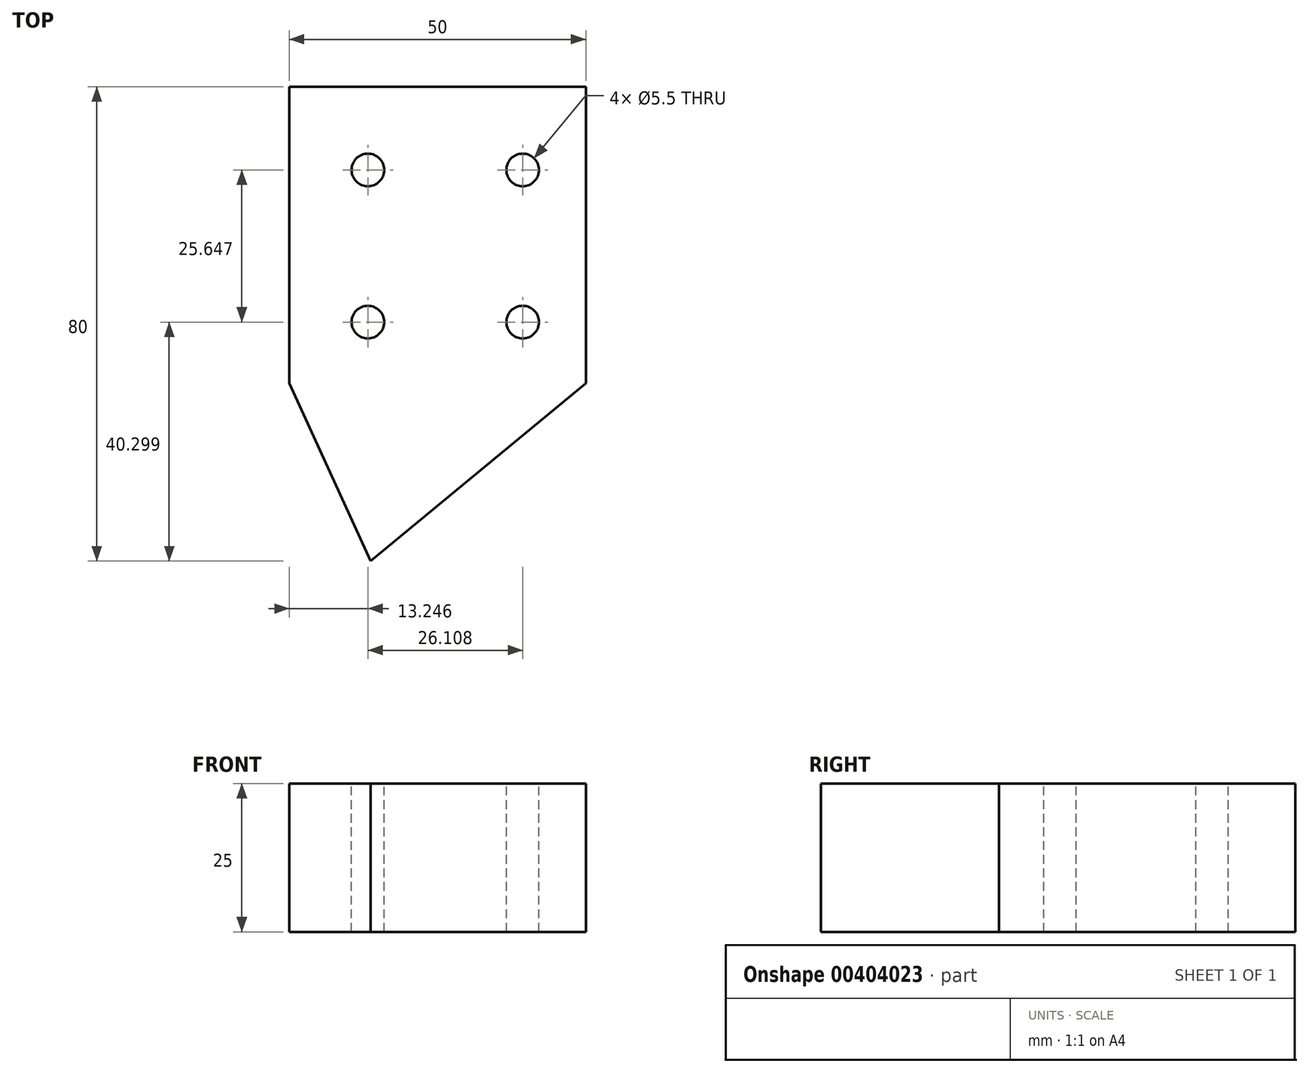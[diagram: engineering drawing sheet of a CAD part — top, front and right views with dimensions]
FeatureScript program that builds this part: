
annotation { "Feature Type Name" : "Feature", "Feature Type Description" : "" }
export const myFeature = defineFeature(function(context is Context, id is Id, definition is map)
    precondition{}
    {
        {
            var Q0;
            Q0=qCreatedBy(makeId("Top.planeOp"),FACE);
            var sketch = newSketch(context, id + "F0", { "sketchPlane" : qUnion([Q0])});
            skLineSegment(sketch, "E0", {"start": v(0, 0) * mm, "end": v(0, 50) * mm});
            skLineSegment(sketch, "E1", {"start": v(0, 50) * mm, "end": v(50, 50) * mm});
            skLineSegment(sketch, "E2", {"start": v(50, 50) * mm, "end": v(50, 0) * mm});
            skLineSegment(sketch, "E3", {"start": v(50, 0) * mm, "end": v(13.73, -30) * mm});
            skLineSegment(sketch, "E4", {"start": v(13.73, -30) * mm, "end": v(0, 0) * mm});
            skSolve(sketch);
        }
        {
            var Q0;
            Q0=makeQuery(id+"F0.imprint","IMPRINT",FACE,{"disambiguationData":[TD([[makeQuery(id+"F0.imprint","IMPRINT",EDGE,{"derivedFrom":sQuery(id+"F0.wireOp",EDGE,"E0")}),-1.0]])]});
            extrude(context, id + "F1", {"entities" : qUnion([Q0]), "depth" : 25 * mm});
        }
        {
            var Q0;
            Q0=makeQuery(id+"F1.opExtrude","CAP_FACE",FACE,{"disambiguationData":[OSD([sQuery(id+"F0.wireOp",EDGE,"E0"),sQuery(id+"F0.wireOp",EDGE,"E1"),sQuery(id+"F0.wireOp",EDGE,"E2"),sQuery(id+"F0.wireOp",EDGE,"E3"),sQuery(id+"F0.wireOp",EDGE,"E4")])],"isStart":false});
            var sketch = newSketch(context, id + "F2", { "sketchPlane" : qUnion([Q0])});
            skPoint(sketch, "E5", {"position": v(39.35, 35.95) * mm});
            skPoint(sketch, "E6", {"position": v(13.25, 35.95) * mm});
            skPoint(sketch, "E7", {"position": v(39.35, 10.3) * mm});
            skPoint(sketch, "E8", {"position": v(13.25, 10.3) * mm});
            skSolve(sketch);
        }
        {
            var Q0;
            Q0=sQuery(id+"F2.wireOp",VERTEX,"E6");
            var Q1;
            Q1=sQuery(id+"F2.wireOp",VERTEX,"E5");
            var Q2;
            Q2=sQuery(id+"F2.wireOp",VERTEX,"E7");
            var Q3;
            Q3=sQuery(id+"F2.wireOp",VERTEX,"E8");
            var Q4;
            Q4=makeQuery(id+"F1.opExtrude","SWEPT_BODY",BODY,{"disambiguationData":[OSD([sQuery(id+"F0.wireOp",EDGE,"E0"),sQuery(id+"F0.wireOp",EDGE,"E1"),sQuery(id+"F0.wireOp",EDGE,"E2"),sQuery(id+"F0.wireOp",EDGE,"E3"),sQuery(id+"F0.wireOp",EDGE,"E4")])]});
            hole(context, id + "F3", {"style" : HoleStyle.SIMPLE, "endStyle" : HoleEndStyle.THROUGH, "standardTappedOrClearance" : lookupTablePath({ "standard" : "ISO", "fit" : "Normal", "size" : "M5", "type" : "Clearance" }), "standardBlindInLast" : lookupTablePath({ "fit" : "Standard", "standard" : "ISO", "size" : "M5", "type" : "Clearance" }), "holeDiameter" : 5.5 * mm, "isTappedThrough" : true, "tappedDepth" : 12 * mm, "tapClearance" : 3, "locations" : qUnion([Q0, Q1, Q2, Q3]), "scope" : qUnion([Q4])});
        }
    });
